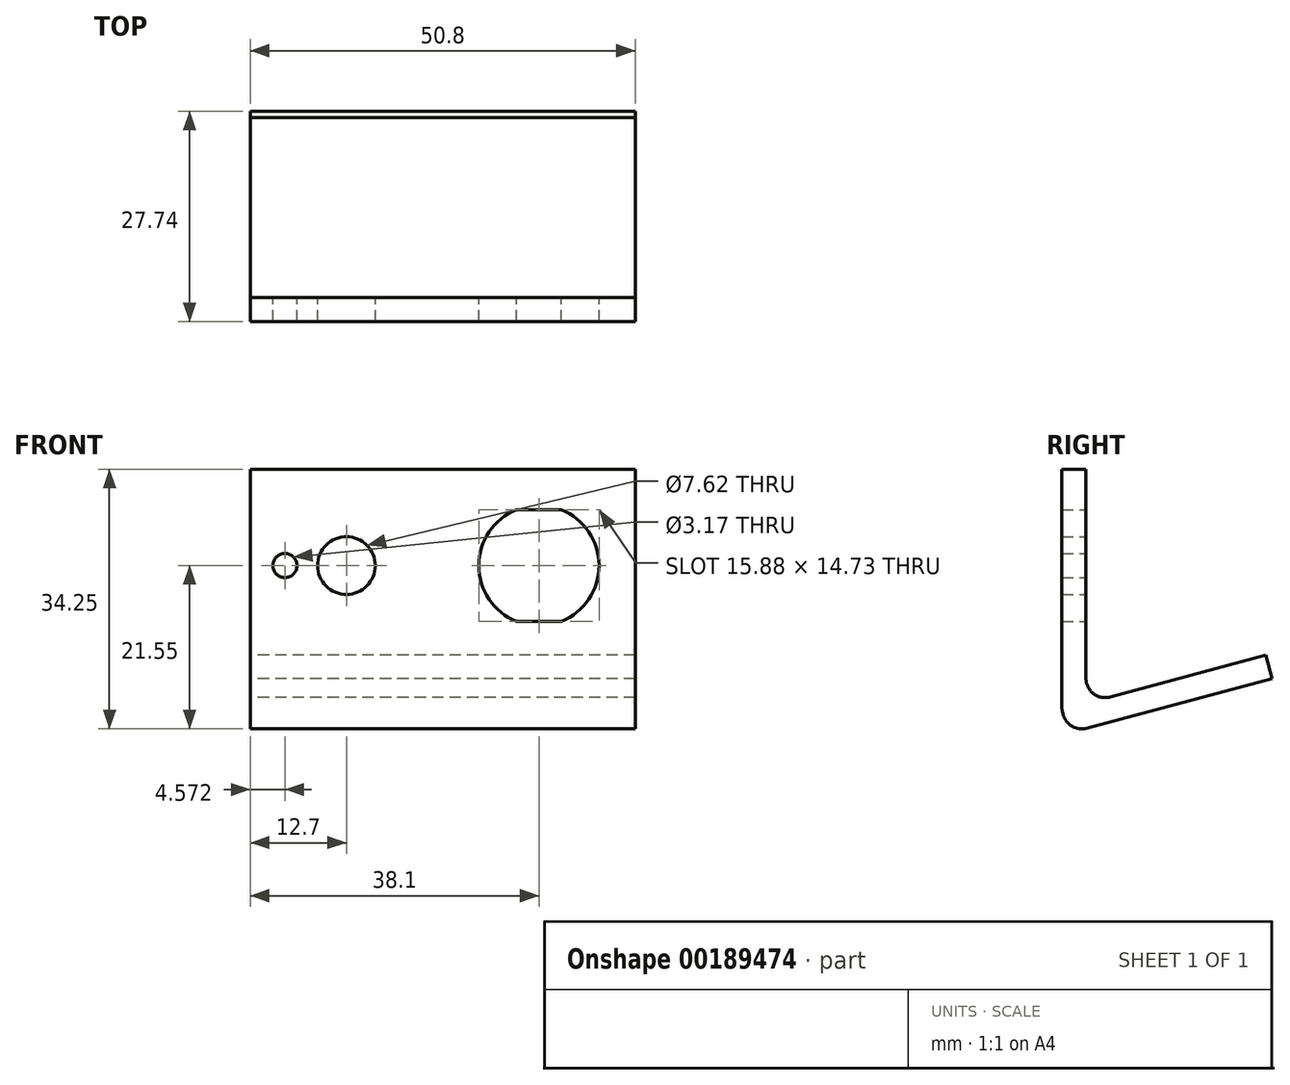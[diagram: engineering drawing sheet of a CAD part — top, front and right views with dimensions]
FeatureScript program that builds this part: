
annotation { "Feature Type Name" : "Feature", "Feature Type Description" : "" }
export const myFeature = defineFeature(function(context is Context, id is Id, definition is map)
    precondition{}
    {
        {
            var Q0;
            Q0=qCreatedBy(makeId("Front.planeOp"),FACE);
            var sketch = newSketch(context, id + "F0", { "sketchPlane" : qUnion([Q0])});
            skPoint(sketch, "E0.middle", {"position": v(0, 0) * mm});
            skCircle(sketch, "E1", {"center": v(-12.7, 0) * mm, "radius": 3.81 * mm});
            skArc(sketch, "E2", {"start": v(9.74, 7.37) * mm, "mid": v(4.76, 0) * mm, "end": v(9.74, -7.37) * mm});
            skLineSegment(sketch, "E3", {"start": v(9.74, 7.37) * mm, "end": v(15.66, 7.37) * mm});
            skLineSegment(sketch, "E4", {"start": v(9.74, -7.37) * mm, "end": v(15.66, -7.37) * mm});
            skArc(sketch, "E5.trimOffspring", {"start": v(15.66, -7.37) * mm, "mid": v(20.64, 0) * mm, "end": v(15.66, 7.37) * mm});
            skCircle(sketch, "E6", {"center": v(-20.83, 0) * mm, "radius": 1.59 * mm});
            skLineSegment(sketch, "E7.bottom", {"start": v(-25.4, 12.7) * mm, "end": v(25.4, 12.7) * mm});
            skLineSegment(sketch, "E7.top", {"start": v(-25.4, -19.05) * mm, "end": v(25.4, -19.05) * mm});
            skLineSegment(sketch, "E7.left", {"start": v(-25.4, 12.7) * mm, "end": v(-25.4, -19.05) * mm});
            skLineSegment(sketch, "E7.right", {"start": v(25.4, 12.7) * mm, "end": v(25.4, -19.05) * mm});
            skSolve(sketch);
        }
        {
            var Q0;
            Q0 = qSketchRegion(id + "F0", true);
            extrude(context, id + "F1", {"entities" : qUnion([Q0]), "depth" : 3.17 * mm});
        }
        {
            var Q0;
            Q0=makeQuery(id+"F1.opExtrude","SWEPT_FACE",FACE,{"disambiguationData":[OSD([sQuery(id+"F0.wireOp",EDGE,"E7.left")])]});
            var sketch = newSketch(context, id + "F2", { "sketchPlane" : qUnion([Q0])});
            skLineSegment(sketch, "E8", {"start": v(3.18, -19.05) * mm, "end": v(-23.74, -11.84) * mm});
            skLineSegment(sketch, "E9", {"start": v(-23.74, -11.84) * mm, "end": v(-24.56, -14.9) * mm});
            skLineSegment(sketch, "E10", {"start": v(-24.56, -14.9) * mm, "end": v(2.35, -22.12) * mm});
            skLineSegment(sketch, "E11", {"start": v(2.35, -22.12) * mm, "end": v(3.18, -19.05) * mm});
            skSolve(sketch);
        }
        {
            var Q0;
            Q0 = qSketchRegion(id + "F2", true);
            var Q1;
            Q1=makeQuery(id+"F1.opExtrude","SWEPT_FACE",FACE,{"disambiguationData":[OSD([sQuery(id+"F0.wireOp",EDGE,"E7.right")])]});
            extrude(context, id + "F3", {"entities" : qUnion([Q0]), "operationType" : NewBodyOperationType.ADD, "endBound" : BoundingType.UP_TO_SURFACE, "oppositeDirection" : true, "endBoundEntityFace" : qUnion([Q1]), "depth" : 25.4 * mm});
        }
        {
            var Q0;
            Q0=makeQuery(id+"F3.boolean.opBoolean","INTERSECT",EDGE,{"derivedFrom":[makeQuery(id+"F1.opExtrude","CAP_FACE",FACE,{"disambiguationData":[OSD([sQuery(id+"F0.wireOp",EDGE,"E1"),sQuery(id+"F0.wireOp",EDGE,"E2"),sQuery(id+"F0.wireOp",EDGE,"E3"),sQuery(id+"F0.wireOp",EDGE,"E4"),sQuery(id+"F0.wireOp",EDGE,"E5.trimOffspring"),sQuery(id+"F0.wireOp",EDGE,"E6"),sQuery(id+"F0.wireOp",EDGE,"E7.bottom"),sQuery(id+"F0.wireOp",EDGE,"E7.top"),sQuery(id+"F0.wireOp",EDGE,"E7.left"),sQuery(id+"F0.wireOp",EDGE,"E7.right")])],"isStart":true}),makeQuery(id+"F3.opExtrude","SWEPT_FACE",FACE,{"disambiguationData":[OSD([sQuery(id+"F2.wireOp",EDGE,"E8")])]})]});
            fillet(context, id + "F4", {"entities" : qUnion([Q0]), "radius" : 2.54 * mm, "tangentPropagation" : true, "allowEdgeOverflow" : false});
        }
        {
            var Q0;
            Q0=makeQuery(id+"F3.opExtrude","SWEPT_EDGE",EDGE,{"disambiguationData":[OSD([sQuery(id+"F2.wireOp",EDGE,"E10"),sQuery(id+"F2.wireOp",EDGE,"E11")])]});
            var Q1;
            {var subQ0=sQuery(id+"F0.wireOp",EDGE,"E7.top");Q1=makeQuery(id+"F3.boolean.opBoolean","MERGE",EDGE,{"derivedFrom":[makeQuery(id+"F1.opExtrude","CAP_EDGE",EDGE,{"disambiguationData":[OSD([subQ0])],"isStart":false}),makeQuery(id+"F3.opExtrude","SWEPT_EDGE",EDGE,{"disambiguationData":[OSD([subQ0,sQuery(id+"F0.wireOp",EDGE,"E7.left"),sQuery(id+"F2.wireOp",EDGE,"E8"),sQuery(id+"F2.wireOp",EDGE,"E11")])]})]});}
            fillet(context, id + "F5", {"entities" : qUnion([Q0, Q1]), "radius" : 2.54 * mm, "tangentPropagation" : true, "allowEdgeOverflow" : false});
        }
    });
